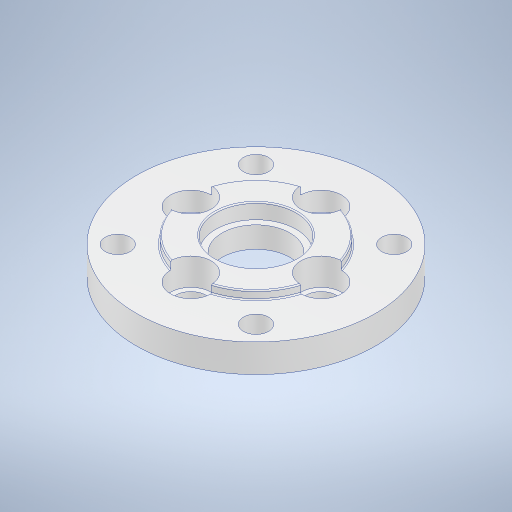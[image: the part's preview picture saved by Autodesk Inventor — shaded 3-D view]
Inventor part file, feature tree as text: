
AUTODESK INVENTOR PART (.ipt)
format: ipt  version: 2023.2 (Build 272271000, 271)  size: 347,136 bytes
history: native  units: in
note: dims shown in document units (in); Inventor stores cm internally (conversion verified against a paired STEP export)
features: extrude x6, sketch x6, fillet x1
ambient origin geometry x8: Origin, YZ Plane, XZ Plane, XY Plane, X Axis, Y Axis, Z Axis, Center Point
bodies: Solid1 (feature_tree)
feature tree (13):
  extrude  "Extrusion1"  Depth=0.2461in
  extrude  "Extrusion2"  Depth=0.1024in
  extrude  "Extrusion3"  Depth=0.2913in
  extrude  "Extrusion4"  Depth=0.8661in
  extrude  "Extrusion5"  Depth=0.2362in
  extrude  "Extrusion6"  TaperAngle=0.0deg  [1 undecoded]
  fillet  "Fillet1"  Radius=0.1476in
  sketch  "Sketch1"  dims[d0=0.8661in d1=0.2461in]
  sketch  "Sketch2"  dims[d2=0.1024in d3=0.0in d4=0.4921in]
  sketch  "Sketch3"  dims[d5=0.0295in d6=0.0in d7=0.2913in]
  sketch  "Sketch4"  dims[d8=0.0551in d9=0.0in d10=0.8661in]
  sketch  "Sketch5"  dims[d11=0.1102in d12=0.2362in]
  sketch  "Sketch6"  dims[d13=1.5748in d15=360.0deg d17=0.0in d18=0.0in d19=0.1476in d20=1.5748in d22=360.0deg d24=0.0984in d25=0.0in d26=135.0deg d27=0.7087in d28=0.0906in d29=1.5748in d31=360.0deg d33=0.0in d34=0.0in d35=0.0039in]
note: 1 required parameter value undecoded (feature->parameter linkage not recoverable at this tier; creation-order binding heuristic only, values carry confidence <= 0.55)
